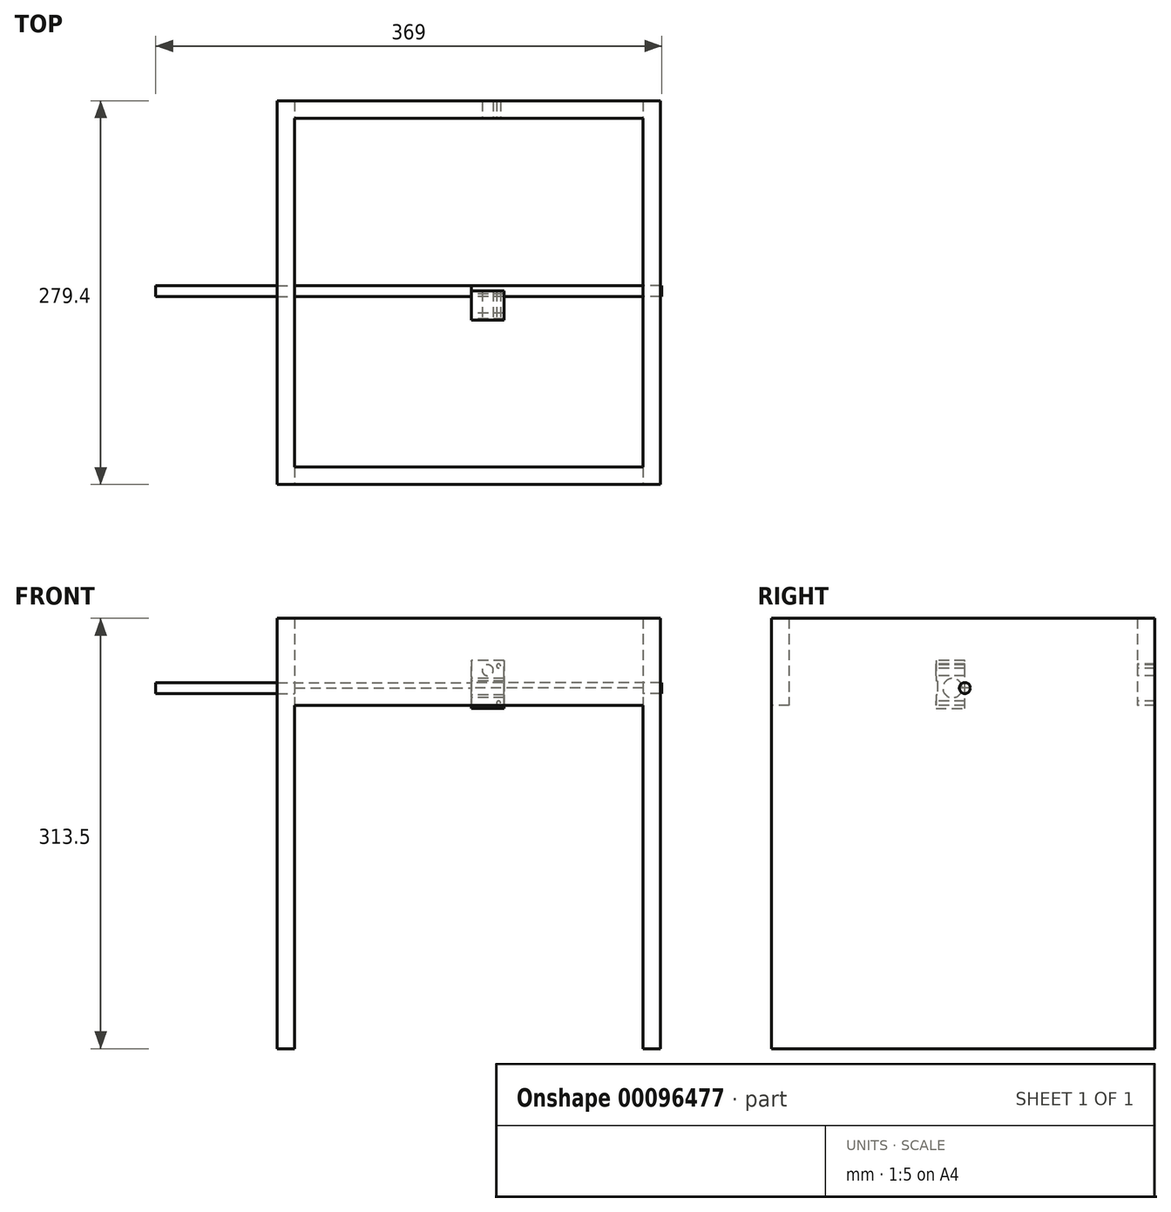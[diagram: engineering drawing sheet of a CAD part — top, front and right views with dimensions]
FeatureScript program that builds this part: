
annotation { "Feature Type Name" : "Feature", "Feature Type Description" : "" }
export const myFeature = defineFeature(function(context is Context, id is Id, definition is map)
    precondition{}
    {
        {
            var Q0;
            Q0=qCreatedBy(makeId("Top.planeOp"),FACE);
            var sketch = newSketch(context, id + "F0", { "sketchPlane" : qUnion([Q0])});
            skLineSegment(sketch, "E0.bottom", {"start": v(-128.63, 125.84) * mm, "end": v(125.37, 125.84) * mm});
            skLineSegment(sketch, "E0.top", {"start": v(-128.63, -128.16) * mm, "end": v(125.37, -128.16) * mm});
            skLineSegment(sketch, "E0.left", {"start": v(-128.63, 125.84) * mm, "end": v(-128.63, -128.16) * mm});
            skLineSegment(sketch, "E0.right", {"start": v(125.37, 125.84) * mm, "end": v(125.37, -128.16) * mm});
            skSolve(sketch);
        }
        {
            var Q0;
            Q0=makeQuery(id+"F0.imprint","IMPRINT",FACE,{"disambiguationData":[TD([[makeQuery(id+"F0.imprint","IMPRINT",EDGE,{"derivedFrom":sQuery(id+"F0.wireOp",EDGE,"E0.bottom")}),-1.0]])]});
            extrude(context, id + "F1", {"entities" : qUnion([Q0]), "depth" : 50.8 * mm});
        }
        {
            var Q0;
            Q0=makeQuery(id+"F1.opExtrude","CAP_FACE",FACE,{"disambiguationData":[OSD([sQuery(id+"F0.wireOp",EDGE,"E0.bottom"),sQuery(id+"F0.wireOp",EDGE,"E0.top"),sQuery(id+"F0.wireOp",EDGE,"E0.left"),sQuery(id+"F0.wireOp",EDGE,"E0.right")])],"isStart":false});
            shell(context, id + "F2", {"entities" : qUnion([Q0]), "thickness" : 12.7 * mm, "oppositeDirection" : true});
        }
        {
            var Q0;
            Q0=qCreatedBy(makeId("Right.planeOp"),FACE);
            var sketch = newSketch(context, id + "F3", { "sketchPlane" : qUnion([Q0])});
            skCircle(sketch, "E1", {"center": v(0, 0) * mm, "radius": 4 * mm});
            skSolve(sketch);
        }
        {
            var Q0;
            Q0=makeQuery(id+"F3.imprint","IMPRINT",FACE,{"disambiguationData":[TD([[makeQuery(id+"F3.imprint","IMPRINT",EDGE,{"derivedFrom":sQuery(id+"F3.wireOp",EDGE,"E1")}),1.0]])]});
            extrude(context, id + "F4", {"entities" : qUnion([Q0]), "depth" : 139 * mm});
        }
        {
            var Q0;
            Q0=makeQuery(id+"F4.opExtrude","CAP_FACE",FACE,{"disambiguationData":[OSD([sQuery(id+"F3.wireOp",EDGE,"E1")])],"isStart":true});
            extrude(context, id + "F5", {"entities" : qUnion([Q0]), "depth" : 230 * mm});
        }
        {
            var Q0;
            Q0=makeQuery(id+"F2.opShell","OFFSET_FACE",FACE,{"disambiguationData":[OSD([sQuery(id+"F0.wireOp",EDGE,"E0.bottom"),sQuery(id+"F0.wireOp",EDGE,"E0.top"),sQuery(id+"F0.wireOp",EDGE,"E0.left"),sQuery(id+"F0.wireOp",EDGE,"E0.right")])]});
            extrude(context, id + "F6", {"entities" : qUnion([Q0]), "operationType" : NewBodyOperationType.REMOVE, "endBound" : BoundingType.THROUGH_ALL, "oppositeDirection" : true, "depth" : 25 * mm});
        }
        {
            var Q0;
            Q0=qCreatedBy(makeId("Right.planeOp"),FACE);
            var sketch = newSketch(context, id + "F7", { "sketchPlane" : qUnion([Q0])});
            skLineSegment(sketch, "E2", {"start": v(0, 20) * mm, "end": v(-21, 20) * mm});
            skLineSegment(sketch, "E3", {"start": v(-21, 20) * mm, "end": v(-21, 5) * mm});
            skLineSegment(sketch, "E4", {"start": v(-21, -15) * mm, "end": v(0, -15) * mm});
            skLineSegment(sketch, "E5.bottom", {"start": v(-20.1, 5) * mm, "end": v(-21, 5) * mm});
            skLineSegment(sketch, "E5.top", {"start": v(-21, -5) * mm, "end": v(-21, -5) * mm});
            skLineSegment(sketch, "E6.trimOffspring", {"start": v(-21, -5) * mm, "end": v(-21, -15) * mm});
            skLineSegment(sketch, "E7", {"start": v(-21, 5) * mm, "end": v(-20.1, 5) * mm});
            skLineSegment(sketch, "E8", {"start": v(-20.1, 5) * mm, "end": v(-20.1, -5) * mm});
            skLineSegment(sketch, "E9", {"start": v(-20.1, -5) * mm, "end": v(-21, -5) * mm});
            skCircle(sketch, "E10", {"center": v(-9, 0) * mm, "radius": 7.03 * mm});
            skLineSegment(sketch, "E11", {"start": v(0, -15) * mm, "end": v(0, 20) * mm});
            skLineSegment(sketch, "E12", {"start": v(-9, 0) * mm, "end": v(-20.1, 0) * mm, "construction": true});
            skSolve(sketch);
        }
        {
            var Q0;
            Q0=makeQuery(id+"F7.imprint","IMPRINT",FACE,{"disambiguationData":[TD([[makeQuery(id+"F7.imprint","IMPRINT",EDGE,{"derivedFrom":sQuery(id+"F7.wireOp",EDGE,"E2")}),1.0]])]});
            extrude(context, id + "F8", {"entities" : qUnion([Q0]), "depth" : 24 * mm});
        }
        {
            var Q0;
            Q0=makeQuery(id+"F8.opExtrude","SWEPT_FACE",FACE,{"disambiguationData":[OSD([sQuery(id+"F7.wireOp",EDGE,"E3")])]});
            var sketch = newSketch(context, id + "F9", { "sketchPlane" : qUnion([Q0])});
            skCircle(sketch, "E13", {"center": v(20, 16) * mm, "radius": 1.5 * mm});
            skCircle(sketch, "E14", {"center": v(20, -11) * mm, "radius": 1.5 * mm});
            skCircle(sketch, "E15", {"center": v(12, 13) * mm, "radius": 4.05 * mm});
            skPoint(sketch, "E15.centerSnap0", {"position": v(12, 20) * mm});
            skSolve(sketch);
        }
        {
            var Q0;
            Q0=qSketchRegion(id+"F9",true);
            extrude(context, id + "F10", {"entities" : qUnion([Q0]), "operationType" : NewBodyOperationType.REMOVE, "endBound" : BoundingType.THROUGH_ALL, "oppositeDirection" : true, "depth" : 25.4 * mm});
        }
        {
            var Q0;
            Q0=makeQuery(id+"F1.opExtrude","CAP_FACE",FACE,{"disambiguationData":[OSD([sQuery(id+"F0.wireOp",EDGE,"E0.bottom"),sQuery(id+"F0.wireOp",EDGE,"E0.top"),sQuery(id+"F0.wireOp",EDGE,"E0.left"),sQuery(id+"F0.wireOp",EDGE,"E0.right")])],"isStart":true});
            var sketch = newSketch(context, id + "F11", { "sketchPlane" : qUnion([Q0])});
            skLineSegment(sketch, "E16", {"start": v(125.37, 128.16) * mm, "end": v(125.37, 140.86) * mm});
            skLineSegment(sketch, "E17", {"start": v(125.37, -125.84) * mm, "end": v(125.37, -138.54) * mm});
            skLineSegment(sketch, "E18", {"start": v(-128.63, 128.16) * mm, "end": v(-128.63, 140.86) * mm});
            skLineSegment(sketch, "E19", {"start": v(-128.63, -125.84) * mm, "end": v(-128.63, -138.54) * mm});
            skSolve(sketch);
        }
        {
            var Q0;
            {var subQ6=sQuery(id+"F11.wireOp",EDGE,"E18");Q0=makeQuery(id+"F11.imprint","IMPRINT",FACE,{"disambiguationData":[TD([[makeQuery(id+"F11.imprint","IMPRINT",EDGE,{"derivedFrom":subQ6}),1.0]])]});}
            var Q1;
            {var subQ5=sQuery(id+"F11.wireOp",EDGE,"E16");Q1=makeQuery(id+"F11.imprint","IMPRINT",FACE,{"disambiguationData":[TD([[makeQuery(id+"F11.imprint","IMPRINT",EDGE,{"derivedFrom":subQ5}),-1.0]])]});}
            extrude(context, id + "F12", {"entities" : qUnion([Q0, Q1]), "operationType" : NewBodyOperationType.ADD, "depth" : 250 * mm});
        }
    });
